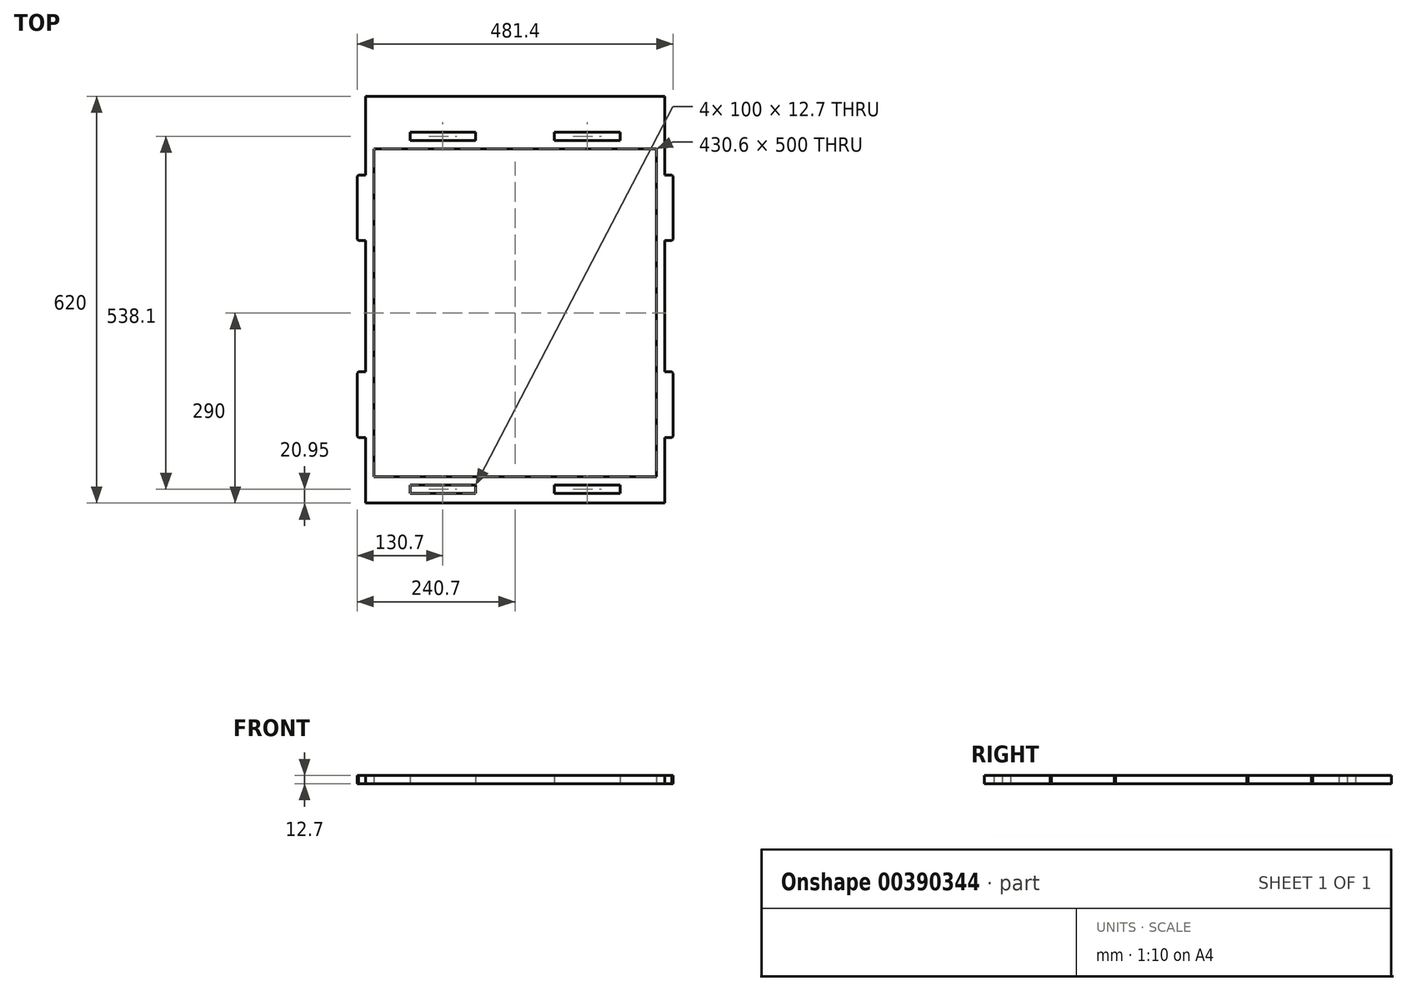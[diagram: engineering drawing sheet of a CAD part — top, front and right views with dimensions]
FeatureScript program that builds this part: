
annotation { "Feature Type Name" : "Feature", "Feature Type Description" : "" }
export const myFeature = defineFeature(function(context is Context, id is Id, definition is map)
    precondition{}
    {
        {
            var Q0;
            Q0=qCreatedBy(makeId("Top.planeOp"),FACE);
            var sketch = newSketch(context, id + "F0", { "sketchPlane" : qUnion([Q0])});
            skLineSegment(sketch, "E0.bottom", {"start": v(228, -310) * mm, "end": v(-228, -310) * mm});
            skLineSegment(sketch, "E0.top", {"start": v(228, 310) * mm, "end": v(-228, 310) * mm});
            skLineSegment(sketch, "E0.left", {"start": v(228, -310) * mm, "end": v(228, -210) * mm});
            skLineSegment(sketch, "E0.right", {"start": v(-228, -310) * mm, "end": v(-228, -210) * mm});
            skPoint(sketch, "E0.middle", {"position": v(0, 0) * mm});
            skLineSegment(sketch, "E1.bottom", {"start": v(215.3, -270) * mm, "end": v(-215.3, -270) * mm});
            skLineSegment(sketch, "E1.top", {"start": v(215.3, 230) * mm, "end": v(-215.3, 230) * mm});
            skLineSegment(sketch, "E1.left", {"start": v(215.3, -270) * mm, "end": v(215.3, 230) * mm});
            skLineSegment(sketch, "E1.right", {"start": v(-215.3, -270) * mm, "end": v(-215.3, 230) * mm});
            skLineSegment(sketch, "E2", {"start": v(0, 230) * mm, "end": v(0, 0) * mm, "construction": true});
            skLineSegment(sketch, "E3.bottom", {"start": v(-240.7, -110) * mm, "end": v(-228, -110) * mm});
            skLineSegment(sketch, "E3.top", {"start": v(-240.7, -210) * mm, "end": v(-228, -210) * mm});
            skLineSegment(sketch, "E3.left", {"start": v(-240.7, -110) * mm, "end": v(-240.7, -210) * mm});
            skLineSegment(sketch, "E4.trimOffspring", {"start": v(-228, -110) * mm, "end": v(-228, 90) * mm});
            skLineSegment(sketch, "E5", {"start": v(-228, -10) * mm, "end": v(228, -10) * mm, "construction": true});
            skLineSegment(sketch, "E6", {"start": v(-228, -110) * mm, "end": v(228, -110) * mm, "construction": true});
            skLineSegment(sketch, "E7.MirrorCS", {"start": v(-240.7, 90) * mm, "end": v(-228, 90) * mm});
            skLineSegment(sketch, "E8.MirrorCS", {"start": v(-240.7, 90) * mm, "end": v(-240.7, 190) * mm});
            skLineSegment(sketch, "E9.MirrorCS", {"start": v(-240.7, 190) * mm, "end": v(-228, 190) * mm});
            skLineSegment(sketch, "E10.trimOffspring", {"start": v(-228, 190) * mm, "end": v(-228, 310) * mm});
            skLineSegment(sketch, "E11.MirrorCS", {"start": v(240.7, -110) * mm, "end": v(228, -110) * mm});
            skLineSegment(sketch, "E12.MirrorCS", {"start": v(240.7, -110) * mm, "end": v(240.7, -210) * mm});
            skLineSegment(sketch, "E13.MirrorCS", {"start": v(240.7, -210) * mm, "end": v(228, -210) * mm});
            skLineSegment(sketch, "E14.MirrorCS", {"start": v(240.7, 190) * mm, "end": v(228, 190) * mm});
            skLineSegment(sketch, "E15.MirrorCS", {"start": v(240.7, 90) * mm, "end": v(240.7, 190) * mm});
            skLineSegment(sketch, "E16.MirrorCS", {"start": v(240.7, 90) * mm, "end": v(228, 90) * mm});
            skLineSegment(sketch, "E17.trimOffspring", {"start": v(228, 190) * mm, "end": v(228, 310) * mm});
            skLineSegment(sketch, "E18.trimOffspring", {"start": v(228, -110) * mm, "end": v(228, 90) * mm});
            skLineSegment(sketch, "E19", {"start": v(-228, 242.7) * mm, "end": v(228, 242.7) * mm, "construction": true});
            skLineSegment(sketch, "E20.bottom", {"start": v(-160, 255.4) * mm, "end": v(-60, 255.4) * mm});
            skLineSegment(sketch, "E20.top", {"start": v(-160, 242.7) * mm, "end": v(-60, 242.7) * mm});
            skLineSegment(sketch, "E20.left", {"start": v(-160, 255.4) * mm, "end": v(-160, 242.7) * mm});
            skLineSegment(sketch, "E20.right", {"start": v(-60, 255.4) * mm, "end": v(-60, 242.7) * mm});
            skLineSegment(sketch, "E21.MirrorCS", {"start": v(60, 255.4) * mm, "end": v(60, 242.7) * mm});
            skLineSegment(sketch, "E22.MirrorCS", {"start": v(160, 255.4) * mm, "end": v(160, 242.7) * mm});
            skLineSegment(sketch, "E23.MirrorCS", {"start": v(160, 242.7) * mm, "end": v(60, 242.7) * mm});
            skLineSegment(sketch, "E24.MirrorCS", {"start": v(160, 255.4) * mm, "end": v(60, 255.4) * mm});
            skLineSegment(sketch, "E25", {"start": v(-228, -282.7) * mm, "end": v(228, -282.7) * mm, "construction": true});
            skLineSegment(sketch, "E26.bottom", {"start": v(-160, -282.7) * mm, "end": v(-60, -282.7) * mm});
            skLineSegment(sketch, "E26.top", {"start": v(-160, -295.4) * mm, "end": v(-60, -295.4) * mm});
            skLineSegment(sketch, "E26.left", {"start": v(-160, -282.7) * mm, "end": v(-160, -295.4) * mm});
            skLineSegment(sketch, "E26.right", {"start": v(-60, -282.7) * mm, "end": v(-60, -295.4) * mm});
            skLineSegment(sketch, "E27.MirrorCS", {"start": v(160, -295.4) * mm, "end": v(60, -295.4) * mm});
            skLineSegment(sketch, "E28.MirrorCS", {"start": v(160, -282.7) * mm, "end": v(60, -282.7) * mm});
            skLineSegment(sketch, "E29.MirrorCS", {"start": v(60, -282.7) * mm, "end": v(60, -295.4) * mm});
            skLineSegment(sketch, "E30.MirrorCS", {"start": v(160, -282.7) * mm, "end": v(160, -295.4) * mm});
            skSolve(sketch);
        }
        {
            var Q0;
            Q0 = qSketchRegion(id + "F0", true);
            extrude(context, id + "F1", {"entities" : qUnion([Q0]), "depth" : 12.7 * mm});
        }
        {
            var Q0;
            Q0=makeQuery(id+"F1.opExtrude","SWEPT_EDGE",EDGE,{"disambiguationData":[OSD([sQuery(id+"F0.wireOp",EDGE,"E11.MirrorCS"),sQuery(id+"F0.wireOp",EDGE,"E12.MirrorCS")])]});
            var Q1;
            Q1=makeQuery(id+"F1.opExtrude","SWEPT_EDGE",EDGE,{"disambiguationData":[OSD([sQuery(id+"F0.wireOp",EDGE,"E12.MirrorCS"),sQuery(id+"F0.wireOp",EDGE,"E13.MirrorCS")])]});
            var Q2;
            Q2=makeQuery(id+"F1.opExtrude","SWEPT_EDGE",EDGE,{"disambiguationData":[OSD([sQuery(id+"F0.wireOp",EDGE,"E14.MirrorCS"),sQuery(id+"F0.wireOp",EDGE,"E15.MirrorCS")])]});
            var Q3;
            Q3=makeQuery(id+"F1.opExtrude","SWEPT_EDGE",EDGE,{"disambiguationData":[OSD([sQuery(id+"F0.wireOp",EDGE,"E15.MirrorCS"),sQuery(id+"F0.wireOp",EDGE,"E16.MirrorCS")])]});
            var Q4;
            Q4=makeQuery(id+"F1.opExtrude","SWEPT_EDGE",EDGE,{"disambiguationData":[OSD([sQuery(id+"F0.wireOp",EDGE,"E8.MirrorCS"),sQuery(id+"F0.wireOp",EDGE,"E9.MirrorCS")])]});
            var Q5;
            Q5=makeQuery(id+"F1.opExtrude","SWEPT_EDGE",EDGE,{"disambiguationData":[OSD([sQuery(id+"F0.wireOp",EDGE,"E7.MirrorCS"),sQuery(id+"F0.wireOp",EDGE,"E8.MirrorCS")])]});
            var Q6;
            Q6=makeQuery(id+"F1.opExtrude","SWEPT_EDGE",EDGE,{"disambiguationData":[OSD([sQuery(id+"F0.wireOp",EDGE,"E3.bottom"),sQuery(id+"F0.wireOp",EDGE,"E3.left")])]});
            var Q7;
            Q7=makeQuery(id+"F1.opExtrude","SWEPT_EDGE",EDGE,{"disambiguationData":[OSD([sQuery(id+"F0.wireOp",EDGE,"E3.top"),sQuery(id+"F0.wireOp",EDGE,"E3.left")])]});
            chamfer(context, id + "F2", {"entities" : qUnion([Q0, Q1, Q2, Q3, Q4, Q5, Q6, Q7]), "width" : 2 * mm, "tangentPropagation" : true});
        }
    });
